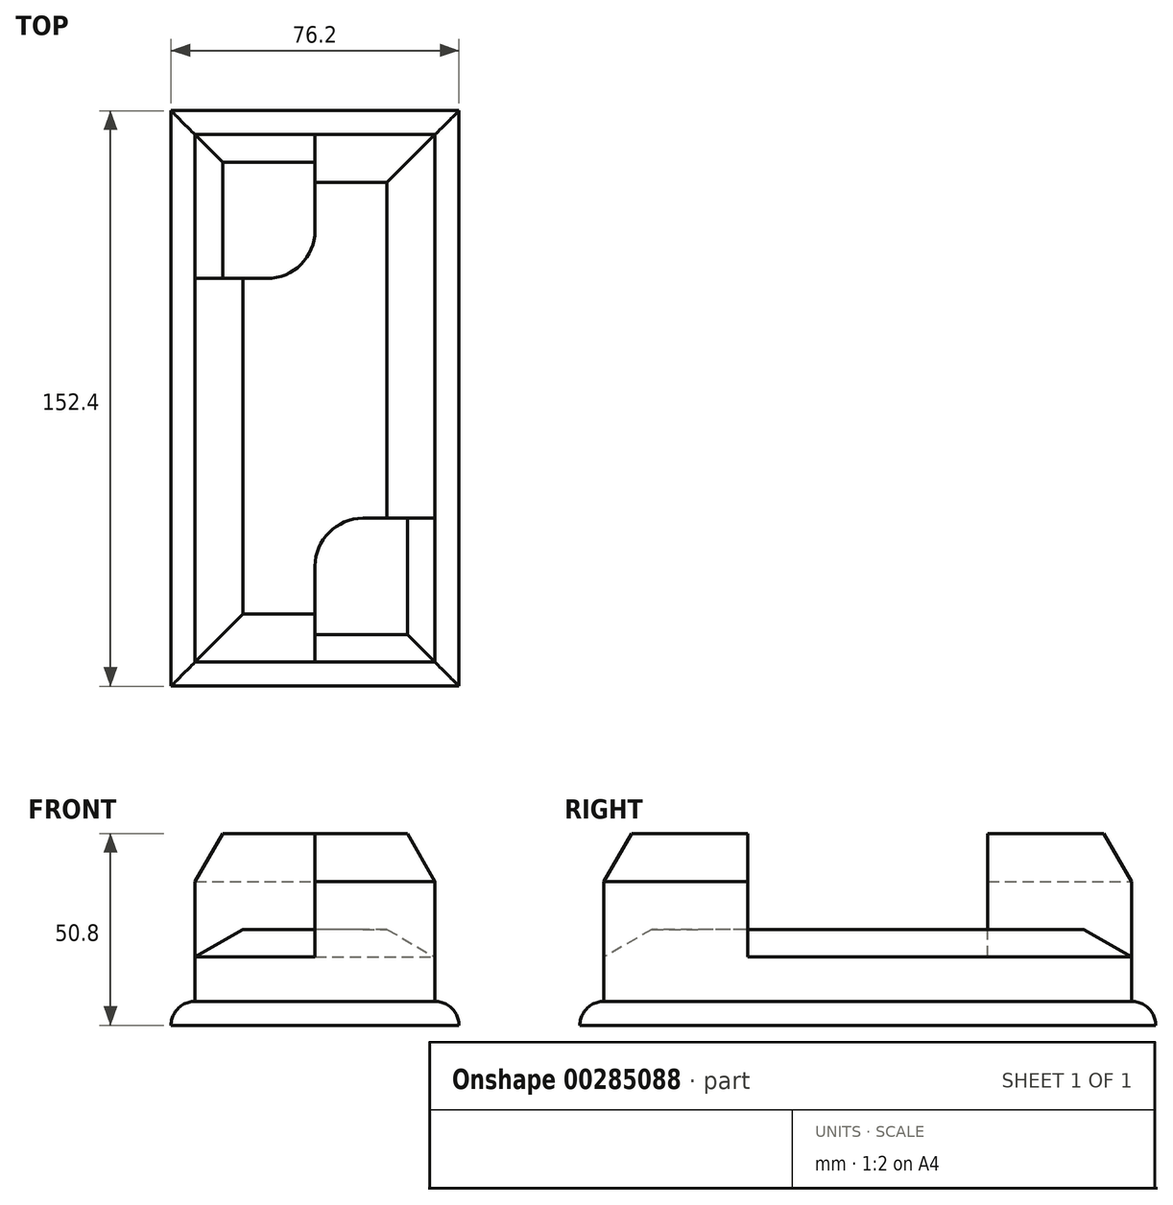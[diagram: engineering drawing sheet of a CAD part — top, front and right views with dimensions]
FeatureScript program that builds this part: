
annotation { "Feature Type Name" : "Feature", "Feature Type Description" : "" }
export const myFeature = defineFeature(function(context is Context, id is Id, definition is map)
    precondition{}
    {
        {
            var Q0;
            Q0=qCreatedBy(makeId("Top.planeOp"),FACE);
            var sketch = newSketch(context, id + "F0", { "sketchPlane" : qUnion([Q0])});
            skLineSegment(sketch, "E0.bottom", {"start": v(-31.75, 89.87) * mm, "end": v(44.45, 89.87) * mm});
            skLineSegment(sketch, "E0.top", {"start": v(-31.75, -62.53) * mm, "end": v(44.45, -62.53) * mm});
            skLineSegment(sketch, "E0.left", {"start": v(-31.75, 89.87) * mm, "end": v(-31.75, -62.53) * mm});
            skLineSegment(sketch, "E0.right", {"start": v(44.45, 89.87) * mm, "end": v(44.45, -62.53) * mm});
            skLineSegment(sketch, "E1.0", {"start": v(-25.4, 83.52) * mm, "end": v(38.1, 83.52) * mm});
            skLineSegment(sketch, "E1.1", {"start": v(-25.4, 83.52) * mm, "end": v(-25.4, -56.18) * mm});
            skLineSegment(sketch, "E1.2", {"start": v(-25.4, -56.18) * mm, "end": v(38.1, -56.18) * mm});
            skLineSegment(sketch, "E1.3", {"start": v(38.1, 83.52) * mm, "end": v(38.1, -56.18) * mm});
            skPoint(sketch, "E2.start.orphan", {"position": v(0, 83.52) * mm});
            skPoint(sketch, "E3.start.orphan", {"position": v(0, -56.18) * mm});
            skLineSegment(sketch, "E4", {"start": v(6.35, -56.18) * mm, "end": v(6.35, -30.78) * mm});
            skLineSegment(sketch, "E5", {"start": v(19.05, -18.08) * mm, "end": v(38.1, -18.08) * mm});
            skPoint(sketch, "E6.visualSharp", {"position": v(6.35, -18.08) * mm});
            skArc(sketch, "E6.filletArc", {"start": v(19.05, -18.08) * mm, "mid": v(10.07, -21.8) * mm, "end": v(6.35, -30.78) * mm});
            skLineSegment(sketch, "E7", {"start": v(6.35, 83.52) * mm, "end": v(6.35, 58.12) * mm});
            skPoint(sketch, "E7.endSnap0", {"position": v(6.35, 83.52) * mm});
            skLineSegment(sketch, "E8", {"start": v(-6.35, 45.42) * mm, "end": v(-31.75, 45.42) * mm});
            skPoint(sketch, "E9.visualSharp", {"position": v(6.35, 45.42) * mm});
            skArc(sketch, "E9.filletArc", {"start": v(-6.35, 45.42) * mm, "mid": v(2.63, 49.14) * mm, "end": v(6.35, 58.12) * mm});
            skSolve(sketch);
        }
        {
            var Q0;
            {var subQ10=sQuery(id+"F0.wireOp",EDGE,"E0.bottom");Q0=makeQuery(id+"F0.imprint","IMPRINT",FACE,{"disambiguationData":[TD([[makeQuery(id+"F0.imprint","IMPRINT",EDGE,{"derivedFrom":subQ10}),-1.0]])]});}
            extrude(context, id + "F1", {"entities" : qUnion([Q0]), "depth" : 6.35 * mm});
        }
        {
            var Q0;
            {var subQ3=sQuery(id+"F0.wireOp",EDGE,"E4");Q0=makeQuery(id+"F0.imprint","IMPRINT",FACE,{"disambiguationData":[TD([[makeQuery(id+"F0.imprint","IMPRINT",EDGE,{"derivedFrom":subQ3}),1.0]])]});}
            extrude(context, id + "F2", {"entities" : qUnion([Q0]), "operationType" : NewBodyOperationType.ADD, "depth" : 25.4 * mm});
        }
        {
            var Q0;
            {var subQ0=sQuery(id+"F0.wireOp",EDGE,"E7");Q0=makeQuery(id+"F0.imprint","IMPRINT",FACE,{"disambiguationData":[TD([[makeQuery(id+"F0.imprint","IMPRINT",EDGE,{"derivedFrom":subQ0}),-1.0]])]});}
            var Q1;
            {var subQ1=sQuery(id+"F0.wireOp",EDGE,"E4");Q1=makeQuery(id+"F0.imprint","IMPRINT",FACE,{"disambiguationData":[TD([[makeQuery(id+"F0.imprint","IMPRINT",EDGE,{"derivedFrom":subQ1}),-1.0]])]});}
            extrude(context, id + "F3", {"entities" : qUnion([Q0, Q1]), "operationType" : NewBodyOperationType.ADD, "depth" : 50.8 * mm});
        }
        {
            var Q0;
            Q0=makeQuery(id+"F3.opExtrude","CAP_EDGE",EDGE,{"disambiguationData":[OSD([sQuery(id+"F0.wireOp",EDGE,"E1.0")])],"isStart":false});
            var Q1;
            Q1=makeQuery(id+"F3.opExtrude","CAP_EDGE",EDGE,{"disambiguationData":[OSD([sQuery(id+"F0.wireOp",EDGE,"E1.1")])],"isStart":false});
            chamfer(context, id + "F4", {"entities" : qUnion([Q0, Q1]), "chamferType" : ChamferType.OFFSET_ANGLE, "width" : 12.7 * mm, "oppositeDirection" : false, "angle" : 30 * degree, "tangentPropagation" : true});
        }
        {
            var Q0;
            Q0=makeQuery(id+"F3.opExtrude","CAP_EDGE",EDGE,{"disambiguationData":[OSD([sQuery(id+"F0.wireOp",EDGE,"E1.3")])],"isStart":false});
            var Q1;
            Q1=makeQuery(id+"F3.opExtrude","CAP_EDGE",EDGE,{"disambiguationData":[OSD([sQuery(id+"F0.wireOp",EDGE,"E1.2")])],"isStart":false});
            chamfer(context, id + "F5", {"entities" : qUnion([Q0, Q1]), "chamferType" : ChamferType.OFFSET_ANGLE, "width" : 12.7 * mm, "oppositeDirection" : false, "angle" : 30 * degree, "tangentPropagation" : true});
        }
        {
            var Q0;
            Q0=makeQuery(id+"F2.opExtrude","CAP_EDGE",EDGE,{"disambiguationData":[OSD([sQuery(id+"F0.wireOp",EDGE,"E1.1")])],"isStart":false});
            var Q1;
            Q1=makeQuery(id+"F2.opExtrude","CAP_EDGE",EDGE,{"disambiguationData":[OSD([sQuery(id+"F0.wireOp",EDGE,"E1.2")])],"isStart":false});
            var Q2;
            Q2=makeQuery(id+"F2.opExtrude","CAP_EDGE",EDGE,{"disambiguationData":[OSD([sQuery(id+"F0.wireOp",EDGE,"E1.3")])],"isStart":false});
            var Q3;
            Q3=makeQuery(id+"F2.opExtrude","CAP_EDGE",EDGE,{"disambiguationData":[OSD([sQuery(id+"F0.wireOp",EDGE,"E1.0")])],"isStart":false});
            chamfer(context, id + "F6", {"entities" : qUnion([Q0, Q1, Q2, Q3]), "chamferType" : ChamferType.OFFSET_ANGLE, "width" : 12.7 * mm, "oppositeDirection" : false, "angle" : 30 * degree, "tangentPropagation" : true});
        }
        {
            var Q0;
            Q0=makeQuery(id+"F1.opExtrude","CAP_EDGE",EDGE,{"disambiguationData":[OSD([sQuery(id+"F0.wireOp",EDGE,"E0.right")])],"isStart":false});
            var Q1;
            Q1=makeQuery(id+"F1.opExtrude","CAP_EDGE",EDGE,{"disambiguationData":[OSD([sQuery(id+"F0.wireOp",EDGE,"E0.top")])],"isStart":false});
            var Q2;
            Q2=makeQuery(id+"F1.opExtrude","CAP_EDGE",EDGE,{"disambiguationData":[OSD([sQuery(id+"F0.wireOp",EDGE,"E0.left")])],"isStart":false});
            var Q3;
            Q3=makeQuery(id+"F1.opExtrude","CAP_EDGE",EDGE,{"disambiguationData":[OSD([sQuery(id+"F0.wireOp",EDGE,"E0.bottom")])],"isStart":false});
            fillet(context, id + "F7", {"entities" : qUnion([Q0, Q1, Q2, Q3]), "radius" : 6.35 * mm, "tangentPropagation" : true, "allowEdgeOverflow" : false});
        }
    });
